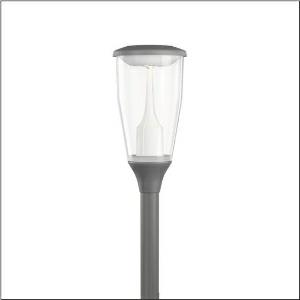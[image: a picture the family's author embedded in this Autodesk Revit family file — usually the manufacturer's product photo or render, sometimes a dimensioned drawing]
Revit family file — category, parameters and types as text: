
# Revit family: dl_11_iq___p1_0a_5xa5565ff14h000022_0ce9
name_source: partatom
category: Lighting Fixtures
units: mm (PartAtom-declared; Revit-internal decimal feet)

## family parameters
Cut with Voids When Loaded = No
Host = Face
Light Source = No
Part Type = Normal
Room Calculation Point = No
Round Connector Dimension = Use Diameter
Shared = No

## types (1)
- --- (1 x LED, 1530 lm, 10.5 W, 3000K)
    Apparent Load = 11 VA
    CIE Flux Codes = 34 63 91 95 100
    Color Rendering = 70
    Color Temperature = 3000K
    Default Elevation = 1800 mm
    Description = DL 11 iQ, mast luminaire, Module 540 iQ-SR, primary light control with 3 zone facetted reflector, of plastic, silver coated, highly specular, structured, primary optical cover: cover, of PMMA, transparent, light distribution: P1.0a, light emission: direct distribution, primary light characteristic: asymmetric, installation type: post-top, LED, High Power LED, rated luminous flux: 1.560lm, luminous efficacy: 149lm/W, light colour: 730, colour temperature: 3000K, control gear: iQ Street-Remote, control: Street-Remote, Auto-Match, Temp-Guard, Lumen-Switch, Night-Set, Smart-Wire, Light-Fading, Desk-Remote (wireless, voltage-free reading and setting of iQ features in the workshop via application-optimized NFC function/RFID function), optimised constant luminous flux control (CLO 2.0), mains connection: 220..240V, AC, 50/60Hz, connection cable pre-assembled, cable length: 5,5m, start of lifetime: 10W, end of service life: 11W, reduction: 5W, luminaire housing, upper part, of diecast aluminium, coated, Siteco® metallic grey (DB 702S), spigot size: 60mm (post-top), mounting height: 3..5m, post-top mast mounting element, of diecast aluminium, coated, Siteco® metallic grey (DB 702S), Module 540 iQ-SR, traffic white (RAL 9016), equipment: standard, protection rating (complete): IP66, insulation class (complete): insulation class II (safety insulation), certification: CE, ENEC, ENEC+, VDE, impact resistance: IK07, packaging unit: 1 piece

Light Distribution: P1.0a
    Height = 665 mm
    Lamp = 1 x LED
    Lamp Light Flux = 1530 lm
    Lamp Power = 10.5 W
    Lamp count = 1
    Length = 334 mm
    Luminous efficacy = 146 lm/W
    Manufacturer = Siteco
    ModVariant = No
    Model = 5XA5565FF14H000022
    Number of Poles = 1
    OnlyDefault = Yes
    Power Factor = 1
    Product Name = DL 11 iQ | P1.0a
    Product group = mast luminaire | pylon top
    ProductGroupID = 6100
    Protection Class = Protection class II
    Protection Degree = IP 66
    RLX_Detail_Level = 1
    RLX_Emergency_Light_Flux = 0 lm
    RLX_Emergency_Type = 0
    RLX_Emergency_Type_DB = No
    RlxData = <blob elided: 103877 chars, md5=4add5d9a>
    Socket = socket
    Standby Power = 0 W
    System Light Flux = 1530 lm
    System Power = 11 W
    Type Comments = factory setting: luminous flux: 100 % | dim-lin: 254 | 419 mA
    Type Image = l_1258354.jpg
    URL = http://relux.com
    VarID = @adj_091818
    Voltage = 0 V
    Weight = 0.00 kg
    Width = 0 mm  [stored 0 ft]

note: [stored X ft] marks values corroborated as IEEE doubles in the binary element streams (Revit-internal decimal feet)

## geometry (parser evidence)
native form markers: Blend x4, Sweep x11
no freeform markers — native parametric forms only
